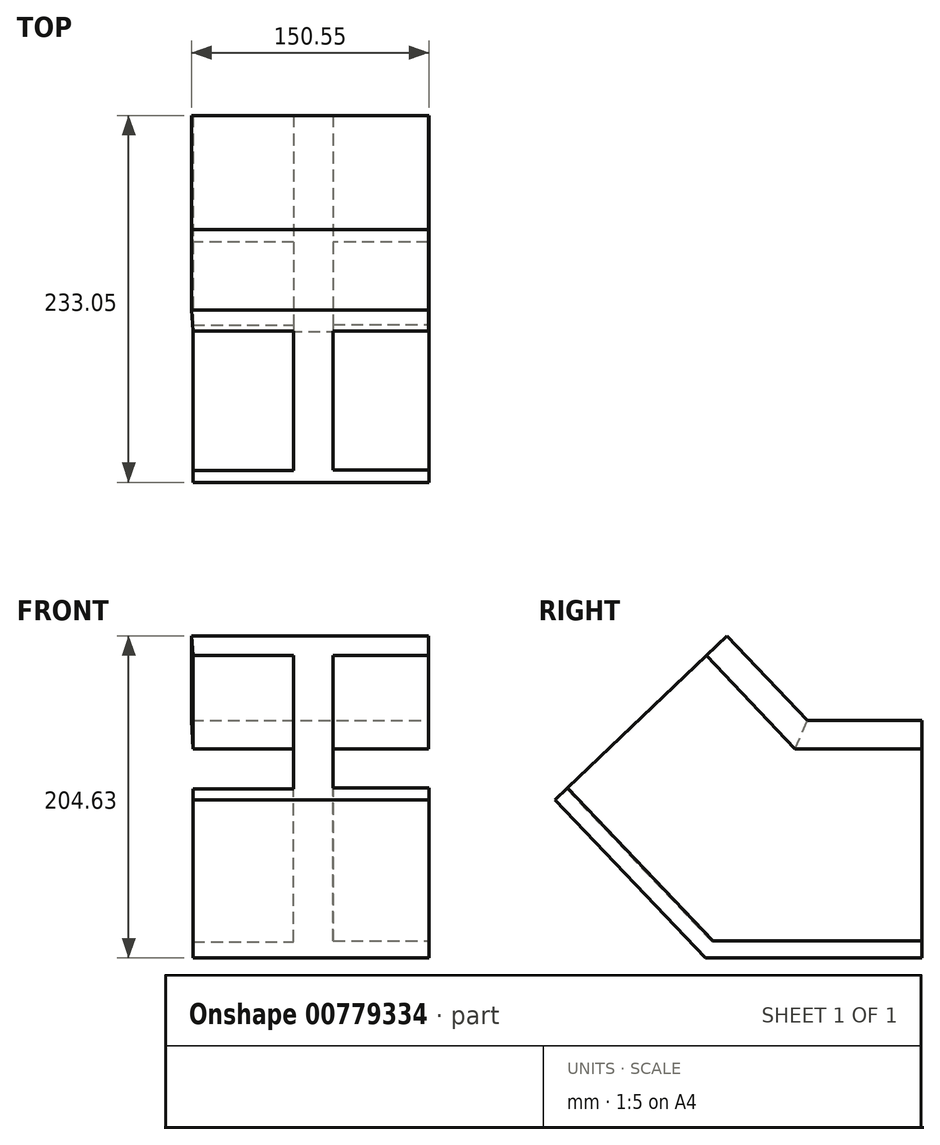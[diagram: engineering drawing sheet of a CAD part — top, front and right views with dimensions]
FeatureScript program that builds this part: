
annotation { "Feature Type Name" : "Feature", "Feature Type Description" : "" }
export const myFeature = defineFeature(function(context is Context, id is Id, definition is map)
    precondition{}
    {
        {
            var Q0;
            Q0=qCreatedBy(makeId("Front.planeOp"),FACE);
            var sketch = newSketch(context, id + "F0", { "sketchPlane" : qUnion([Q0])});
            skLineSegment(sketch, "E0", {"start": v(-75.66, 76.3) * mm, "end": v(74.63, 76.3) * mm});
            skLineSegment(sketch, "E1", {"start": v(74.63, 76.3) * mm, "end": v(74.63, 58.12) * mm});
            skLineSegment(sketch, "E2", {"start": v(74.63, 58.12) * mm, "end": v(14.2, 58.12) * mm});
            skLineSegment(sketch, "E3", {"start": v(14.2, 58.12) * mm, "end": v(14.2, -63.75) * mm});
            skLineSegment(sketch, "E4", {"start": v(14.2, -63.75) * mm, "end": v(74.89, -63.75) * mm});
            skLineSegment(sketch, "E5", {"start": v(74.89, -63.75) * mm, "end": v(74.89, -74.76) * mm});
            skLineSegment(sketch, "E6", {"start": v(74.89, -74.76) * mm, "end": v(-74.89, -74.76) * mm});
            skLineSegment(sketch, "E7", {"start": v(-74.89, -74.76) * mm, "end": v(-74.89, -64.52) * mm});
            skLineSegment(sketch, "E8", {"start": v(-74.89, -64.52) * mm, "end": v(-10.88, -64.52) * mm});
            skLineSegment(sketch, "E9", {"start": v(-10.88, -64.52) * mm, "end": v(-10.88, 58.12) * mm});
            skLineSegment(sketch, "E10", {"start": v(-10.88, 58.12) * mm, "end": v(-74.78, 58.12) * mm});
            skLineSegment(sketch, "E11", {"start": v(-74.78, 58.12) * mm, "end": v(-75.66, 76.3) * mm});
            skSolve(sketch);
        }
        {
            var Q0;
            Q0=qCreatedBy(makeId("Right.planeOp"),FACE);
            var sketch = newSketch(context, id + "F1", { "sketchPlane" : qUnion([Q0])});
            skLineSegment(sketch, "E12", {"start": v(0, 0) * mm, "end": v(-105.35, 0) * mm});
            skLineSegment(sketch, "E13", {"start": v(-105.35, 0) * mm, "end": v(-178.89, 77.28) * mm});
            skSolve(sketch);
        }
        {
            var Q0;
            Q0=makeQuery(id+"F0.imprint","IMPRINT",FACE,{"disambiguationData":[TD([[makeQuery(id+"F0.imprint","IMPRINT",EDGE,{"derivedFrom":sQuery(id+"F0.wireOp",EDGE,"E0")}),-1.0]])]});
            var Q1;
            Q1=sQuery(id+"F1.wireOp",EDGE,"E12");
            var Q2;
            Q2=sQuery(id+"F1.wireOp",EDGE,"E13");
            sweep(context, id + "F2", {"profiles" : qUnion([Q0]), "path" : qUnion([Q1, Q2])});
        }
    });
